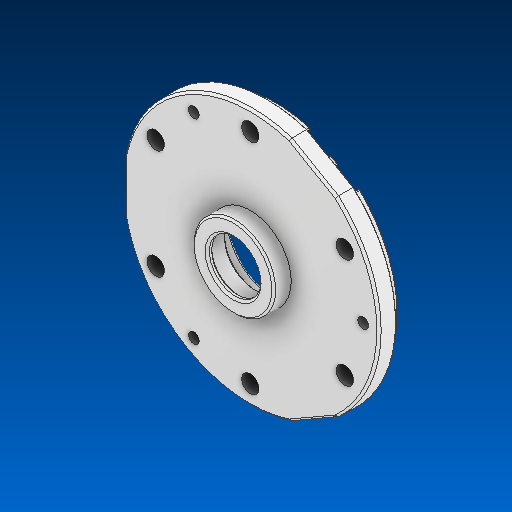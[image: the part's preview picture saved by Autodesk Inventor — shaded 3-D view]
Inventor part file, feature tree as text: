
AUTODESK INVENTOR PART (.ipt)
format: ipt  version: 2022.2 (Build 262287000, 287)  size: 1,240,064 bytes
history: native  units: in
note: dims shown in document units (in); Inventor stores cm internally (conversion verified against a paired STEP export)
features: chamfer x1
ambient origin geometry x8: Origin, YZ Plane, XZ Plane, XY Plane, X Axis, Y Axis, Z Axis, Center Point
bodies: Solid1 (feature_tree)
feature tree (1):
  chamfer  "Chamfer3"  [1 undecoded]
note: 1 required parameter value undecoded (feature->parameter linkage not recoverable at this tier; creation-order binding heuristic only, values carry confidence <= 0.55)
